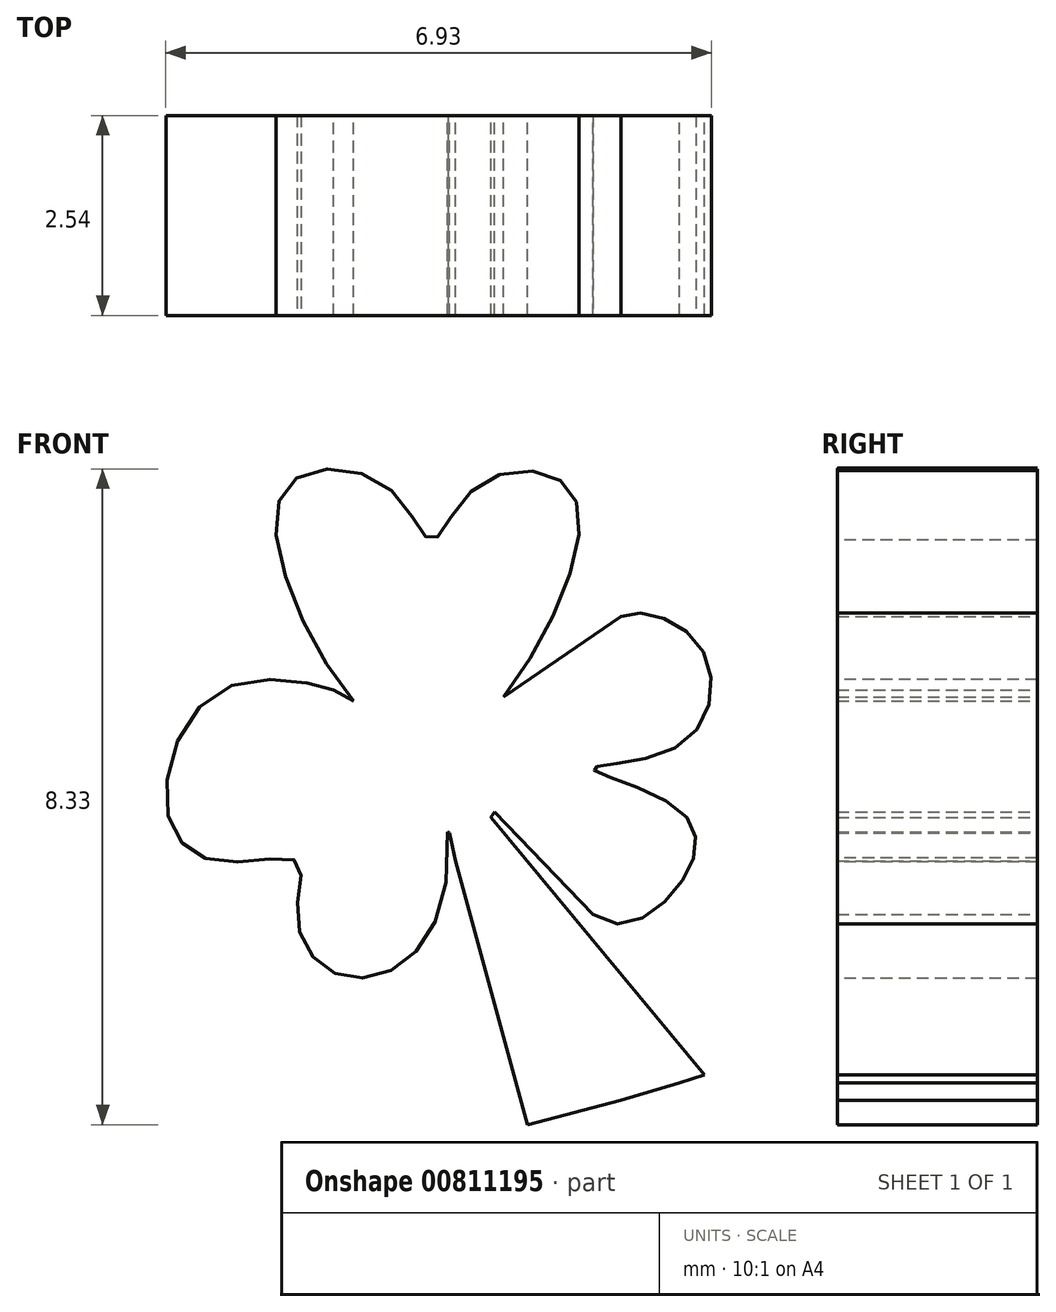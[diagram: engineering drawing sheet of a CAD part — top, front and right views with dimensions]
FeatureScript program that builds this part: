
annotation { "Feature Type Name" : "Feature", "Feature Type Description" : "" }
export const myFeature = defineFeature(function(context is Context, id is Id, definition is map)
    precondition{}
    {
        {
            var Q0;
            Q0=qCreatedBy(makeId("Front.planeOp"),FACE);
            var sketch = newSketch(context, id + "F0", { "sketchPlane" : qUnion([Q0])});
            skPoint(sketch, "E0", {"position": v(-9.07, -3.3) * mm});
            skPoint(sketch, "E1", {"position": v(-9.07, -0.68) * mm});
            skPoint(sketch, "E2", {"position": v(-8.5, 0) * mm});
            skPoint(sketch, "E3", {"position": v(-7.35, 0) * mm});
            skPoint(sketch, "E4", {"position": v(-7.56, -1.7) * mm});
            skPoint(sketch, "E5", {"position": v(-9.65, 0) * mm});
            skPoint(sketch, "E6", {"position": v(-10.9, 0) * mm});
            skPoint(sketch, "E7", {"position": v(-10.54, -2.02) * mm});
            skFitSpline(sketch, "E8", {"points": [v(-9.07, -3.3) * mm, v(-10.54, -2.02) * mm, v(-10.9, 0) * mm, v(-9.65, 0) * mm, v(-9.07, -0.68) * mm, v(-8.5, 0) * mm, v(-7.35, 0) * mm, v(-7.56, -1.7) * mm, v(-9.07, -3.3) * mm]});
            skPoint(sketch, "E9", {"position": v(-33.17, -17.56) * mm});
            skPoint(sketch, "E10", {"position": v(-10.78, -4.77) * mm});
            skPoint(sketch, "E11", {"position": v(-11.74, -4.77) * mm});
            skPoint(sketch, "E12", {"position": v(-12.43, -4.13) * mm});
            skPoint(sketch, "E13", {"position": v(-11.74, -2.59) * mm});
            skPoint(sketch, "E14", {"position": v(-10.78, -5.5) * mm});
            skPoint(sketch, "E15", {"position": v(-10.24, -6.21) * mm});
            skPoint(sketch, "E16", {"position": v(-9.3, -5.95) * mm});
            skFitSpline(sketch, "E17", {"points": [v(-9.07, -3.3) * mm, v(-9.3, -5.95) * mm, v(-10.24, -6.21) * mm, v(-10.78, -5.5) * mm, v(-10.78, -4.77) * mm, v(-11.74, -4.77) * mm, v(-12.43, -4.13) * mm, v(-11.74, -2.59) * mm, v(-10.32, -2.59) * mm], "startDerivative": vector(6.14, -22.07) * mm, "endDerivative": vector(5.67, -1.84) * mm});
            skLineSegment(sketch, "E18", {"start": v(-10.07, -2.73) * mm, "end": v(-10.32, -2.59) * mm});
            skPoint(sketch, "E19", {"position": v(-6.68, -7.8) * mm});
            skPoint(sketch, "E20", {"position": v(-5.92, -7.58) * mm});
            skLineSegment(sketch, "E21", {"start": v(-5.92, -7.58) * mm, "end": v(-6.68, -7.8) * mm});
            skPoint(sketch, "E22", {"position": v(-6.67, -1.65) * mm});
            skPoint(sketch, "E23", {"position": v(-5.68, -2.01) * mm});
            skPoint(sketch, "E24", {"position": v(-5.9, -3.27) * mm});
            skPoint(sketch, "E25", {"position": v(-7.03, -3.59) * mm});
            skPoint(sketch, "E26", {"position": v(-5.9, -4.13) * mm});
            skPoint(sketch, "E27", {"position": v(-5.9, -5.03) * mm});
            skPoint(sketch, "E28", {"position": v(-7.03, -5.44) * mm});
            skFitSpline(sketch, "E29", {"points": [v(-6.67, -1.65) * mm, v(-5.68, -2.01) * mm, v(-5.9, -3.27) * mm, v(-7.03, -3.59) * mm, v(-5.9, -4.13) * mm, v(-5.9, -5.03) * mm, v(-7.03, -5.44) * mm], "startDerivative": vector(4.57, 2.29) * mm, "endDerivative": vector(-7.08, 5.5) * mm});
            skLineSegment(sketch, "E30", {"start": v(-6.67, -1.65) * mm, "end": v(-8.16, -2.68) * mm});
            skLineSegment(sketch, "E31", {"start": v(-7.03, -5.44) * mm, "end": v(-8.27, -4.14) * mm});
            skPoint(sketch, "E32", {"position": v(-7.5, -5.44) * mm});
            skLineSegment(sketch, "E33", {"start": v(-8.84, -4.4) * mm, "end": v(-8.77, -4.76) * mm});
            skLineSegment(sketch, "E34", {"start": v(-8.77, -4.76) * mm, "end": v(-7.85, -8.11) * mm});
            skLineSegment(sketch, "E35", {"start": v(-7.85, -8.11) * mm, "end": v(-6.68, -7.8) * mm});
            skLineSegment(sketch, "E36", {"start": v(-8.32, -4.2) * mm, "end": v(-5.6, -7.48) * mm});
            skLineSegment(sketch, "E37", {"start": v(-5.6, -7.48) * mm, "end": v(-5.92, -7.58) * mm});
            skFitSpline(sketch, "E38", {"points": [v(-8.87, -4.4) * mm, v(-8.27, -4.14) * mm], "startDerivative": vector(0.76, -0.25) * mm, "endDerivative": vector(0.5, 0.75) * mm});
            skSolve(sketch);
        }
        {
            var Q0;
            Q0 = qSketchRegion(id + "F0", true);
            extrude(context, id + "F1", {"entities" : qUnion([Q0]), "depth" : 2.54 * mm, "offsetDistance" : 25.4 * mm});
        }
    });
